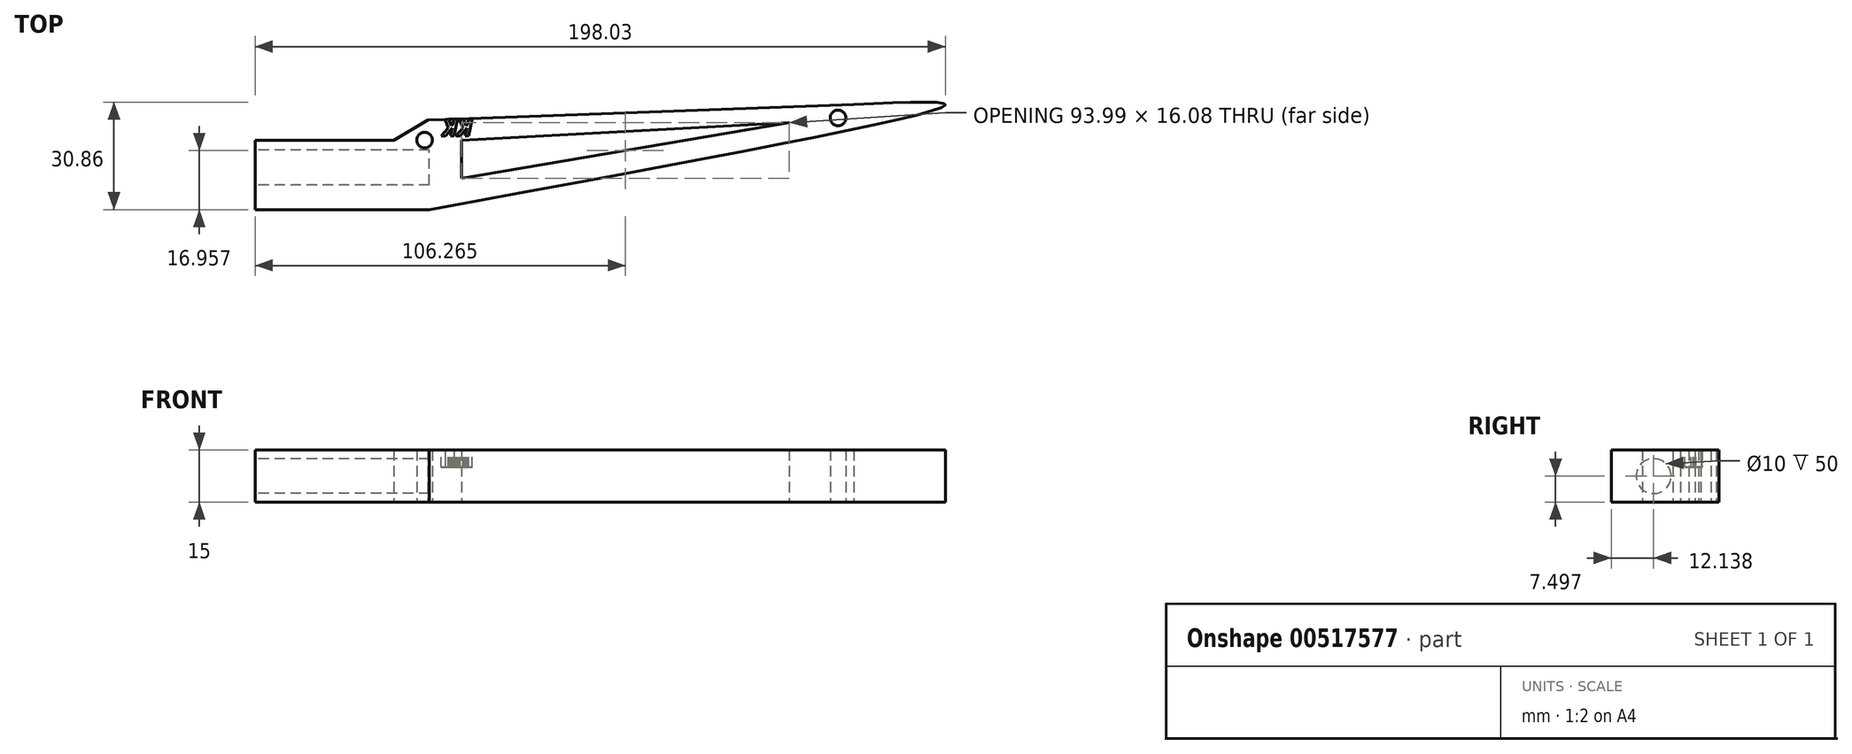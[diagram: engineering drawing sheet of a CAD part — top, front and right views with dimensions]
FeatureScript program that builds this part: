
annotation { "Feature Type Name" : "Feature", "Feature Type Description" : "" }
export const myFeature = defineFeature(function(context is Context, id is Id, definition is map)
    precondition{}
    {
        {
            var Q0;
            Q0=qCreatedBy(makeId("Front.planeOp"),FACE);
            var sketch = newSketch(context, id + "F0", { "sketchPlane" : qUnion([Q0])});
            skLineSegment(sketch, "E0.bottom", {"start": v(-84.2, -32.3) * mm, "end": v(115.8, -32.3) * mm});
            skLineSegment(sketch, "E0.top", {"start": v(-84.2, 17.7) * mm, "end": v(115.8, 17.7) * mm});
            skLineSegment(sketch, "E0.left", {"start": v(-84.2, -32.3) * mm, "end": v(-84.2, 17.7) * mm});
            skLineSegment(sketch, "E0.right", {"start": v(115.8, -32.3) * mm, "end": v(115.8, 17.7) * mm});
            skSolve(sketch);
        }
        {
            var Q0;
            Q0=makeQuery(id+"F0.imprint","IMPRINT",FACE,{"disambiguationData":[TD([[makeQuery(id+"F0.imprint","IMPRINT",EDGE,{"derivedFrom":sQuery(id+"F0.wireOp",EDGE,"E0.bottom")}),1.0]])]});
            extrude(context, id + "F1", {"entities" : qUnion([Q0]), "depth" : 15 * mm, "offsetDistance" : 25 * mm});
        }
        {
            var Q0;
            Q0=makeQuery(id+"F1.opExtrude","SWEPT_FACE",FACE,{"disambiguationData":[OSD([sQuery(id+"F0.wireOp",EDGE,"E0.left")])]});
            var sketch = newSketch(context, id + "F2", { "sketchPlane" : qUnion([Q0])});
            skCircle(sketch, "E1", {"center": v(7.5, 5.56) * mm, "radius": 5 * mm});
            skSolve(sketch);
        }
        {
            var Q0;
            Q0=makeQuery(id+"F2.imprint","IMPRINT",FACE,{"disambiguationData":[TD([[makeQuery(id+"F2.imprint","IMPRINT",EDGE,{"derivedFrom":sQuery(id+"F2.wireOp",EDGE,"7C1XYHwe-JG3x-ZCVl-AM0D-5SnIvYdmpO4R")}),1.0]])]});
            var Q1;
            Q1=makeQuery(id+"F2.imprint","IMPRINT",FACE,{"disambiguationData":[TD([[makeQuery(id+"F2.imprint","IMPRINT",EDGE,{"derivedFrom":sQuery(id+"F2.wireOp",EDGE,"x6kl2QCT-QF8n-Hb51-paJ7-O33Y02bPOw9w")}),1.0]])]});
            var Q2;
            Q2=makeQuery(id+"F2.imprint","IMPRINT",FACE,{"disambiguationData":[TD([[makeQuery(id+"F2.imprint","IMPRINT",EDGE,{"derivedFrom":sQuery(id+"F2.wireOp",EDGE,"cQZxueYZ-TgTE-3FrV-F6xS-BxRsUK2nDiBK")}),1.0]])]});
            var Q3;
            Q3=makeQuery(id+"F2.imprint","IMPRINT",FACE,{"disambiguationData":[TD([[makeQuery(id+"F2.imprint","IMPRINT",EDGE,{"derivedFrom":sQuery(id+"F2.wireOp",EDGE,"E1")}),1.0]])]});
            extrude(context, id + "F3", {"entities" : qUnion([Q0, Q1, Q2, Q3]), "operationType" : NewBodyOperationType.REMOVE, "oppositeDirection" : true, "depth" : 50 * mm, "offsetDistance" : 25 * mm});
        }
        {
            var Q0;
            Q0=makeQuery(id+"F1.opExtrude","CAP_FACE",FACE,{"disambiguationData":[OSD([sQuery(id+"F0.wireOp",EDGE,"E0.bottom"),sQuery(id+"F0.wireOp",EDGE,"E0.top"),sQuery(id+"F0.wireOp",EDGE,"E0.left"),sQuery(id+"F0.wireOp",EDGE,"E0.right")])],"isStart":false});
            var sketch = newSketch(context, id + "F4", { "sketchPlane" : qUnion([Q0])});
            skLineSegment(sketch, "E2", {"start": v(-84.2, -7.3) * mm, "end": v(-44.15, -7.3) * mm});
            skCircle(sketch, "E3", {"center": v(-35.56, -2.25) * mm, "radius": 2.25 * mm});
            skLineSegment(sketch, "E4", {"start": v(-44.4, -2.2) * mm, "end": v(-84.2, -2.2) * mm});
            skPoint(sketch, "E5.1.internal.snap0", {"position": v(115.8, -7.3) * mm});
            skLineSegment(sketch, "E6", {"start": v(-44.4, -2.2) * mm, "end": v(-34.65, -8.05) * mm});
            skLineSegment(sketch, "E7", {"start": v(-24.93, 8.78) * mm, "end": v(-24.93, -2.2) * mm});
            skLineSegment(sketch, "E8", {"start": v(-24.93, -2.2) * mm, "end": v(69.06, -7.3) * mm});
            skPoint(sketch, "E8.endSnap0", {"position": v(-64.18, -7.3) * mm});
            skLineSegment(sketch, "E9", {"start": v(69.06, -7.3) * mm, "end": v(-24.93, 8.78) * mm});
            skLineSegment(sketch, "E10", {"start": v(-34.65, -8.05) * mm, "end": v(87.54, -12.45) * mm});
            skFitSpline(sketch, "E11", {"points": [v(87.54, -12.45) * mm, v(113.83, -12.45) * mm, v(-34.18, 17.7) * mm], "startDerivative": vector(133.32, -6.29) * mm, "endDerivative": vector(-315.27, 57.8) * mm});
            skCircle(sketch, "E12", {"center": v(83.02, -8.64) * mm, "radius": 2.25 * mm});
            skSolve(sketch);
        }
        {
            var Q0;
            Q0=makeQuery(id+"F4.imprint","IMPRINT",FACE,{"disambiguationData":[TD([[makeQuery(id+"F4.imprint","IMPRINT",EDGE,{"derivedFrom":sQuery(id+"F4.wireOp",EDGE,"CTYMIt64-4Dbf-pOx8-GiXN-1BL5Hz3VDo4W")}),1.0]])]});
            var Q1;
            Q1=makeQuery(id+"F4.imprint","IMPRINT",FACE,{"disambiguationData":[TD([[makeQuery(id+"F4.imprint","IMPRINT",EDGE,{"derivedFrom":sQuery(id+"F4.wireOp",EDGE,"E3")}),1.0]])]});
            var Q2;
            Q2=makeQuery(id+"F4.imprint","IMPRINT",FACE,{"disambiguationData":[TD([[makeQuery(id+"F4.imprint","IMPRINT",EDGE,{"derivedFrom":sQuery(id+"F4.wireOp",EDGE,"f7c617ab-3bc9-4f39-92bc-7e6832b7ea1b")}),1.0]])]});
            var Q3;
            Q3=makeQuery(id+"F4.imprint","IMPRINT",FACE,{"disambiguationData":[TD([[makeQuery(id+"F4.imprint","IMPRINT",EDGE,{"derivedFrom":sQuery(id+"F4.wireOp",EDGE,"8c3fd66d-e9d0-4e00-9b48-c57852603eed")}),1.0]])]});
            var Q4;
            {var subQ0=sQuery(id+"F4.wireOp",EDGE,"E2");Q4=makeQuery(id+"F4.imprint","IMPRINT",FACE,{"disambiguationData":[TD([[makeQuery(id+"F4.imprint","IMPRINT",EDGE,{"derivedFrom":subQ0}),-1.0]])]});}
            var Q5;
            {var subQ3=sQuery(id+"F4.wireOp",EDGE,"33581686-948e-46e4-8ad7-1bfde3d96c96");Q5=makeQuery(id+"F4.imprint","IMPRINT",FACE,{"disambiguationData":[TD([[makeQuery(id+"F4.imprint","IMPRINT",EDGE,{"derivedFrom":subQ3}),-1.0]])]});}
            var Q6;
            {var subQ3=sQuery(id+"F4.wireOp",EDGE,"E2");Q6=makeQuery(id+"F4.imprint","IMPRINT",FACE,{"disambiguationData":[TD([[makeQuery(id+"F4.imprint","IMPRINT",EDGE,{"derivedFrom":subQ3}),1.0]])]});}
            var Q7;
            Q7=makeQuery(id+"F4.imprint","IMPRINT",FACE,{"disambiguationData":[TD([[makeQuery(id+"F4.imprint","IMPRINT",EDGE,{"derivedFrom":sQuery(id+"F4.wireOp",EDGE,"DNbrY4DC-MJUu-FtG1-fWDS-qSqdN6B3pgYT")}),1.0]])]});
            var Q8;
            Q8=makeQuery(id+"F4.imprint","IMPRINT",FACE,{"disambiguationData":[TD([[makeQuery(id+"F4.imprint","IMPRINT",EDGE,{"derivedFrom":sQuery(id+"F4.wireOp",EDGE,"E7")}),1.0]])]});
            var Q9;
            Q9=makeQuery(id+"F4.imprint","IMPRINT",FACE,{"disambiguationData":[TD([[makeQuery(id+"F4.imprint","IMPRINT",EDGE,{"derivedFrom":sQuery(id+"F4.wireOp",EDGE,"E12")}),1.0]])]});
            extrude(context, id + "F5", {"entities" : qUnion([Q0, Q1, Q2, Q3, Q4, Q5, Q6, Q7, Q8, Q9]), "operationType" : NewBodyOperationType.REMOVE, "endBound" : BoundingType.THROUGH_ALL, "oppositeDirection" : true, "depth" : 25 * mm, "offsetDistance" : 25 * mm});
        }
        {
            var Q0;
            {var subQ2=sQuery(id+"F4.wireOp",EDGE,"oaDDhET5-kof6-jLvc-aTiG-Ux8WHHciskc8");Q0=makeQuery(id+"F4.imprint","IMPRINT",FACE,{"disambiguationData":[TD([[makeQuery(id+"F4.imprint","IMPRINT",EDGE,{"derivedFrom":subQ2}),1.0]])]});}
            var Q1;
            {var subQ1=sQuery(id+"F4.wireOp",EDGE,"E4");Q1=makeQuery(id+"F4.imprint","IMPRINT",FACE,{"disambiguationData":[TD([[makeQuery(id+"F4.imprint","IMPRINT",EDGE,{"derivedFrom":subQ1}),1.0]])]});}
            extrude(context, id + "F6", {"entities" : qUnion([Q0, Q1]), "operationType" : NewBodyOperationType.REMOVE, "endBound" : BoundingType.THROUGH_ALL, "oppositeDirection" : true, "depth" : 25 * mm, "offsetDistance" : 25 * mm});
        }
        {
            var Q0;
            Q0=makeQuery(id+"F1.opExtrude","CAP_FACE",FACE,{"disambiguationData":[OSD([sQuery(id+"F0.wireOp",EDGE,"E0.bottom"),sQuery(id+"F0.wireOp",EDGE,"E0.top"),sQuery(id+"F0.wireOp",EDGE,"E0.left"),sQuery(id+"F0.wireOp",EDGE,"E0.right")])],"isStart":true});
            var sketch = newSketch(context, id + "F7", { "sketchPlane" : qUnion([Q0])});
            skText(sketch, "E13", { "text": "KK", "fontName": "OpenSans-BoldItalic.ttf"});
            const initialGuessF7  = {"E13": [0.02175, -0.00835, 1, 0, 0.00492]};
            skSetInitialGuess(sketch, initialGuessF7);
            skSolve(sketch);
        }
        {
            var Q0;
            Q0=qSketchRegion(id+"F7",true);
            extrude(context, id + "F8", {"entities" : qUnion([Q0]), "operationType" : NewBodyOperationType.REMOVE, "oppositeDirection" : true, "depth" : 5 * mm, "offsetDistance" : 25 * mm});
        }
        {
            var Q0;
            Q0=makeQuery(id+"F1.opExtrude","SWEPT_BODY",BODY,{"disambiguationData":[OSD([sQuery(id+"F0.wireOp",EDGE,"E0.bottom"),sQuery(id+"F0.wireOp",EDGE,"E0.top"),sQuery(id+"F0.wireOp",EDGE,"E0.left"),sQuery(id+"F0.wireOp",EDGE,"E0.right")])]});
            var Q1;
            Q1=sQuery(id+"F4.wireOp",EDGE,"E4");
            transform(context, id + "F9", {"entities" : qUnion([Q0]), "transformType" : TransformType.ROTATION, "transformAxis" : qUnion([Q1]), "angle" : 90 * degree, "oppositeDirection" : true, "makeCopy" : false});
        }
    });
